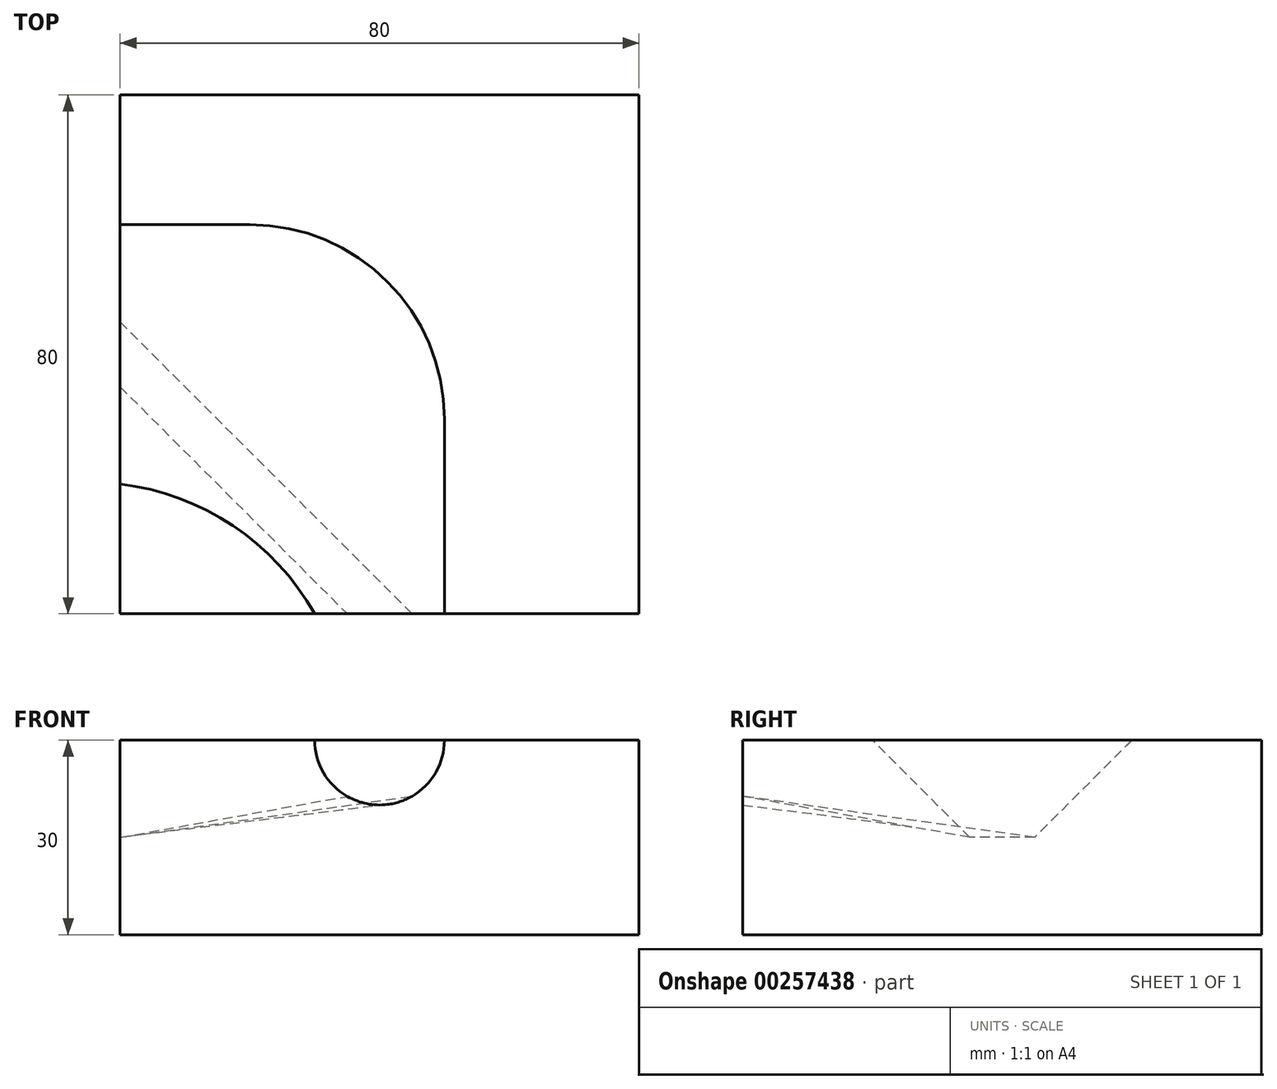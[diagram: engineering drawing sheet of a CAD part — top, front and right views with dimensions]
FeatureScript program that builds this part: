
annotation { "Feature Type Name" : "Feature", "Feature Type Description" : "" }
export const myFeature = defineFeature(function(context is Context, id is Id, definition is map)
    precondition{}
    {
        {
            var Q0;
            Q0=qCreatedBy(makeId("Top.planeOp"),FACE);
            var sketch = newSketch(context, id + "F0", { "sketchPlane" : qUnion([Q0])});
            skLineSegment(sketch, "E0.bottom", {"start": v(-80, 80) * mm, "end": v(0, 80) * mm});
            skLineSegment(sketch, "E0.top", {"start": v(-80, 0) * mm, "end": v(0, 0) * mm});
            skLineSegment(sketch, "E0.left", {"start": v(-80, 80) * mm, "end": v(-80, 0) * mm});
            skLineSegment(sketch, "E0.right", {"start": v(0, 80) * mm, "end": v(0, 0) * mm});
            skSolve(sketch);
        }
        {
            var Q0;
            Q0=makeQuery(id+"F0.imprint","IMPRINT",FACE,{"disambiguationData":[TD([[makeQuery(id+"F0.imprint","IMPRINT",EDGE,{"derivedFrom":sQuery(id+"F0.wireOp",EDGE,"E0.bottom")}),-1.0]])]});
            extrude(context, id + "F1", {"entities" : qUnion([Q0]), "depth" : 30 * mm});
        }
        {
            var Q0;
            Q0=makeQuery(id+"F1.opExtrude","SWEPT_FACE",FACE,{"disambiguationData":[OSD([sQuery(id+"F0.wireOp",EDGE,"E0.left")])]});
            var sketch = newSketch(context, id + "F2", { "sketchPlane" : qUnion([Q0])});
            skLineSegment(sketch, "E1", {"start": v(-60, 30) * mm, "end": v(-45, 15) * mm});
            skLineSegment(sketch, "E2", {"start": v(-45, 15) * mm, "end": v(-35, 15) * mm});
            skLineSegment(sketch, "E3", {"start": v(-35, 15) * mm, "end": v(-20, 30) * mm});
            skLineSegment(sketch, "E4", {"start": v(-20, 30) * mm, "end": v(-60, 30) * mm});
            skLineSegment(sketch, "E5", {"start": v(-40, 15) * mm, "end": v(-40, 43.57) * mm, "construction": true});
            skSolve(sketch);
        }
        {
            var Q0;
            Q0=makeQuery(id+"F1.opExtrude","SWEPT_FACE",FACE,{"disambiguationData":[OSD([sQuery(id+"F0.wireOp",EDGE,"E0.top")])]});
            var sketch = newSketch(context, id + "F3", { "sketchPlane" : qUnion([Q0])});
            skArc(sketch, "E6", {"start": v(-50, 30) * mm, "mid": v(-40, 20) * mm, "end": v(-30, 30) * mm});
            skLineSegment(sketch, "E7", {"start": v(-50, 30) * mm, "end": v(-30, 30) * mm});
            skSolve(sketch);
        }
        {
            var Q0;
            Q0=makeQuery(id+"F1.opExtrude","CAP_FACE",FACE,{"disambiguationData":[OSD([sQuery(id+"F0.wireOp",EDGE,"E0.bottom"),sQuery(id+"F0.wireOp",EDGE,"E0.top"),sQuery(id+"F0.wireOp",EDGE,"E0.left"),sQuery(id+"F0.wireOp",EDGE,"E0.right")])],"isStart":false});
            var sketch = newSketch(context, id + "F4", { "sketchPlane" : qUnion([Q0])});
            skLineSegment(sketch, "E8", {"start": v(-30, 0) * mm, "end": v(-30, 30) * mm});
            skLineSegment(sketch, "E9", {"start": v(-80, 60) * mm, "end": v(-60, 60) * mm});
            skLineSegment(sketch, "E10", {"start": v(-90, 20) * mm, "end": v(-80, 20) * mm, "construction": true});
            skLineSegment(sketch, "E11", {"start": v(-50, -20) * mm, "end": v(-50, 0) * mm, "construction": true});
            skArc(sketch, "E12.filletArc", {"start": v(-30, 30) * mm, "mid": v(-38.79, 51.21) * mm, "end": v(-60, 60) * mm});
            skSolve(sketch);
        }
        {
            var Q0;
            {var subQ3=sQuery(id+"F4.wireOp",EDGE,"E8");Q0=makeQuery(id+"F4.imprint","IMPRINT",FACE,{"disambiguationData":[TD([[makeQuery(id+"F4.imprint","IMPRINT",EDGE,{"derivedFrom":subQ3}),-1.0]])]});}
            var sketch = newSketch(context, id + "F5", { "sketchPlane" : qUnion([Q0])});
            skArc(sketch, "E13", {"start": v(-50, 0) * mm, "mid": v(-62.62, 13.57) * mm, "end": v(-80, 20) * mm});
            skPoint(sketch, "E14", {"position": v(-50, 0) * mm});
            skPoint(sketch, "E15", {"position": v(-80, 20) * mm});
            skSolve(sketch);
        }
        {
            var Q0;
            Q0=makeQuery(id+"F2.imprint","IMPRINT",FACE,{"disambiguationData":[TD([[makeQuery(id+"F2.imprint","IMPRINT",EDGE,{"derivedFrom":sQuery(id+"F2.wireOp",EDGE,"E1")}),1.0]])]});
            var Q1;
            Q1=makeQuery(id+"F3.imprint","IMPRINT",FACE,{"disambiguationData":[TD([[makeQuery(id+"F3.imprint","IMPRINT",EDGE,{"derivedFrom":sQuery(id+"F3.wireOp",EDGE,"E6")}),1.0]])]});
            var Q2;
            Q2 = qConstructionFilter(qBodyType(qCreatedBy(id + "F5" ,EDGE), BodyType.WIRE), ConstructionObject.NO);
            var Q3;
            Q3 = qConstructionFilter(qBodyType(qCreatedBy(id + "F4" ,EDGE), BodyType.WIRE), ConstructionObject.NO);
            loft(context, id + "F6", {"addGuides" : true, "sheetProfilesArray" : [{ "sheetProfileEntities" : qUnion([Q0]) }, { "sheetProfileEntities" : qUnion([Q1]) }], "guidesArray" : [{ "guideEntities" : qUnion([Q2]), "guideDerivativeType" : LoftGuideDerivativeType.DEFAULT, "guideDerivativeMagnitude" : 1 }, { "guideEntities" : qUnion([Q3]), "guideDerivativeType" : LoftGuideDerivativeType.DEFAULT, "guideDerivativeMagnitude" : 1 }]});
        }
    });
